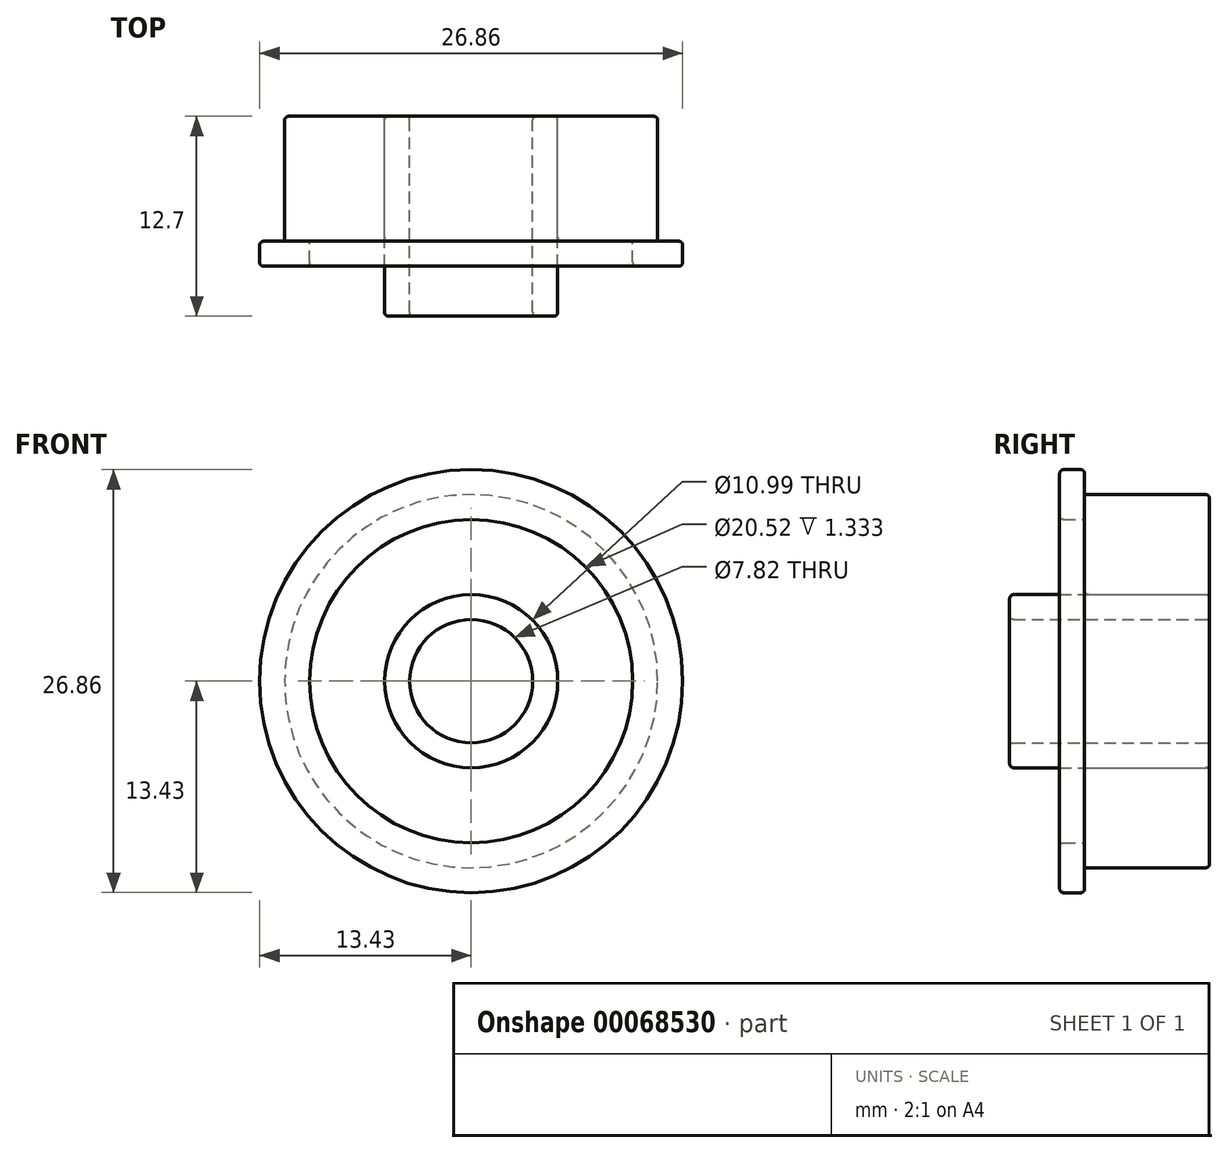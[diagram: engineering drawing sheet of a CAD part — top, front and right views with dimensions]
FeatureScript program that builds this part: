
annotation { "Feature Type Name" : "Feature", "Feature Type Description" : "" }
export const myFeature = defineFeature(function(context is Context, id is Id, definition is map)
    precondition{}
    {
        {
            var Q0;
            Q0=qCreatedBy(makeId("Front.planeOp"),FACE);
            var sketch = newSketch(context, id + "F0", { "sketchPlane" : qUnion([Q0])});
            skCircle(sketch, "E0", {"center": v(0, 0) * mm, "radius": 3.9 * mm});
            skCircle(sketch, "E1", {"center": v(0, 0) * mm, "radius": 5.5 * mm});
            skCircle(sketch, "E2", {"center": v(0, 0) * mm, "radius": 11.85 * mm});
            skCircle(sketch, "E3", {"center": v(0, 0) * mm, "radius": 13.43 * mm});
            skSolve(sketch);
        }
        {
            var Q0;
            Q0=makeQuery(id+"F0.imprint","IMPRINT",FACE,{"disambiguationData":[TD([[makeQuery(id+"F0.imprint","IMPRINT",EDGE,{"derivedFrom":sQuery(id+"F0.wireOp",EDGE,"E0")}),-1.0]])]});
            extrude(context, id + "F1", {"entities" : qUnion([Q0]), "depth" : 12.7 * mm});
        }
        {
            var Q0;
            Q0=makeQuery(id+"F0.imprint","IMPRINT",FACE,{"disambiguationData":[TD([[makeQuery(id+"F0.imprint","IMPRINT",EDGE,{"derivedFrom":sQuery(id+"F0.wireOp",EDGE,"E1")}),-1.0]])]});
            extrude(context, id + "F2", {"entities" : qUnion([Q0]), "depth" : 7.94 * mm});
        }
        {
            var Q0;
            Q0=makeQuery(id+"F2.opExtrude","CAP_FACE",FACE,{"disambiguationData":[OSD([sQuery(id+"F0.wireOp",EDGE,"E1"),sQuery(id+"F0.wireOp",EDGE,"E2")])],"isStart":false});
            var sketch = newSketch(context, id + "F3", { "sketchPlane" : qUnion([Q0])});
            skCircle(sketch, "E4.0", {"center": v(0, 0) * mm, "radius": 11.85 * mm});
            skCircle(sketch, "E5.0", {"center": v(0, 0) * mm, "radius": 13.43 * mm});
            skCircle(sketch, "E6", {"center": v(0, 0) * mm, "radius": 10.26 * mm});
            skSolve(sketch);
        }
        {
            var Q0;
            Q0=makeQuery(id+"F3.imprint","IMPRINT",FACE,{"disambiguationData":[TD([[makeQuery(id+"F3.imprint","IMPRINT",EDGE,{"derivedFrom":sQuery(id+"F3.wireOp",EDGE,"E4.0")}),1.0]])]});
            var Q1;
            Q1=makeQuery(id+"F3.imprint","IMPRINT",FACE,{"disambiguationData":[TD([[makeQuery(id+"F3.imprint","IMPRINT",EDGE,{"derivedFrom":sQuery(id+"F3.wireOp",EDGE,"E4.0")}),-1.0]])]});
            extrude(context, id + "F4", {"entities" : qUnion([Q0, Q1]), "operationType" : NewBodyOperationType.ADD, "depth" : 1.59 * mm});
        }
        {
            var Q0;
            Q0=makeQuery(id+"F4.opExtrude","CAP_EDGE",EDGE,{"disambiguationData":[OSD([sQuery(id+"F3.wireOp",EDGE,"E5.0")])],"isStart":false});
            var Q1;
            Q1=makeQuery(id+"F4.opExtrude","CAP_EDGE",EDGE,{"disambiguationData":[OSD([sQuery(id+"F3.wireOp",EDGE,"E5.0")])],"isStart":true});
            var Q2;
            Q2=makeQuery(id+"F4.opExtrude","CAP_EDGE",EDGE,{"disambiguationData":[OSD([sQuery(id+"F3.wireOp",EDGE,"E6")])],"isStart":false});
            var Q3;
            Q3=makeQuery(id+"F4.opExtrude","CAP_EDGE",EDGE,{"disambiguationData":[OSD([sQuery(id+"F3.wireOp",EDGE,"E6")])],"isStart":true});
            var Q4;
            Q4=makeQuery(id+"F1.opExtrude","CAP_EDGE",EDGE,{"disambiguationData":[OSD([sQuery(id+"F0.wireOp",EDGE,"E1")])],"isStart":false});
            var Q5;
            Q5=makeQuery(id+"F1.opExtrude","CAP_EDGE",EDGE,{"disambiguationData":[OSD([sQuery(id+"F0.wireOp",EDGE,"E0")])],"isStart":false});
            var Q6;
            Q6=makeQuery(id+"F2.opExtrude","CAP_EDGE",EDGE,{"disambiguationData":[OSD([sQuery(id+"F0.wireOp",EDGE,"E1")])],"isStart":false});
            var Q7;
            Q7=makeQuery(id+"F2.opExtrude","CAP_EDGE",EDGE,{"disambiguationData":[OSD([sQuery(id+"F0.wireOp",EDGE,"E2")])],"isStart":true});
            var Q8;
            Q8=makeQuery(id+"F1.opExtrude","CAP_EDGE",EDGE,{"disambiguationData":[OSD([sQuery(id+"F0.wireOp",EDGE,"E1")])],"isStart":true});
            var Q9;
            Q9=makeQuery(id+"F1.opExtrude","CAP_EDGE",EDGE,{"disambiguationData":[OSD([sQuery(id+"F0.wireOp",EDGE,"E0")])],"isStart":true});
            fillet(context, id + "F5", {"entities" : qUnion([Q0, Q1, Q2, Q3, Q4, Q5, Q6, Q7, Q8, Q9]), "radius" : 0.25 * mm, "tangentPropagation" : true, "allowEdgeOverflow" : false});
        }
    });
